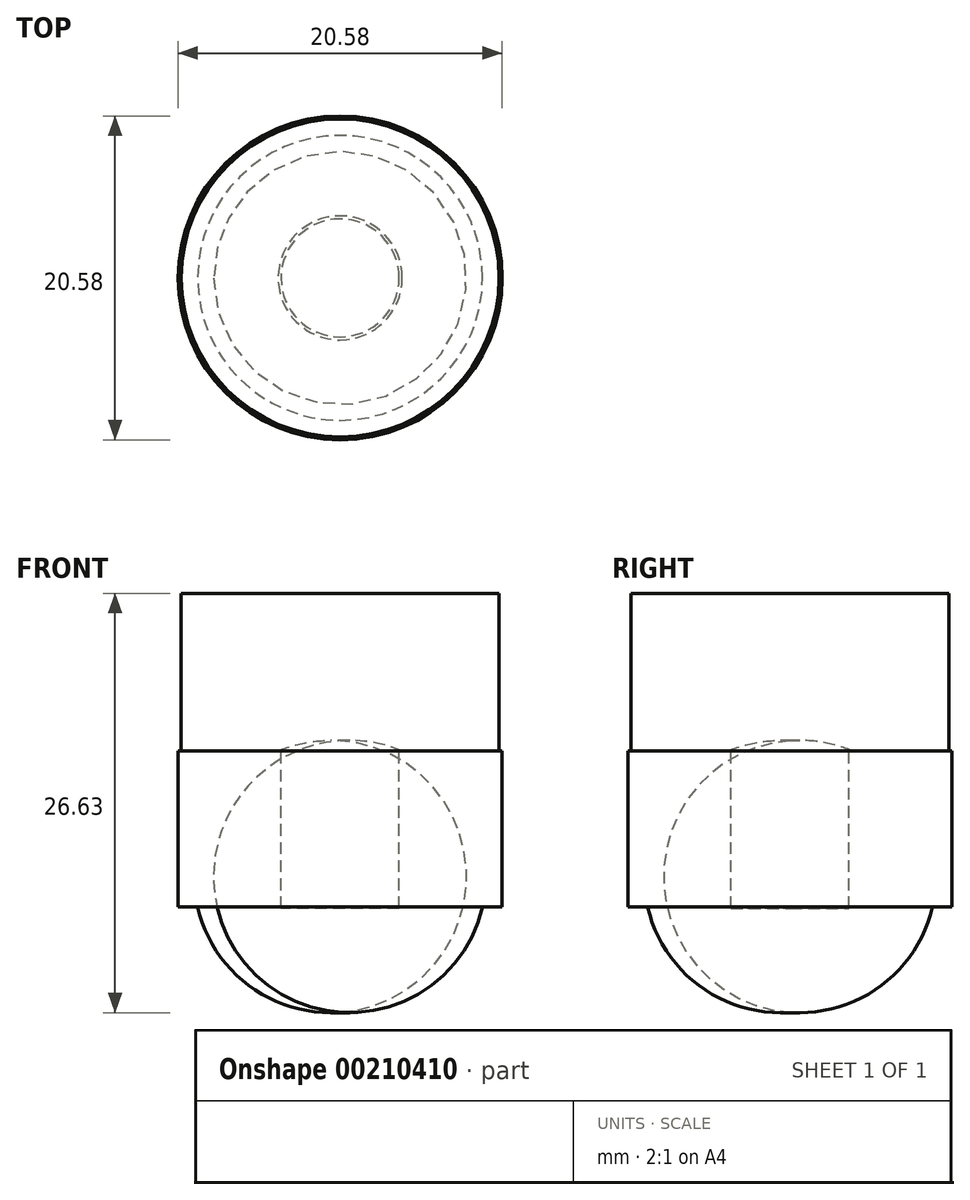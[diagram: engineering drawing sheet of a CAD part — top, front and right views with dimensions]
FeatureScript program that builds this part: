
annotation { "Feature Type Name" : "Feature", "Feature Type Description" : "" }
export const myFeature = defineFeature(function(context is Context, id is Id, definition is map)
    precondition{}
    {
        {
            var Q0;
            Q0=qCreatedBy(makeId("Top.planeOp"),FACE);
            var sketch = newSketch(context, id + "F0", { "sketchPlane" : qUnion([Q0])});
            skCircle(sketch, "E0", {"center": v(0, 0) * mm, "radius": 10.1 * mm});
            skSolve(sketch);
        }
        {
            var Q0;
            Q0=makeQuery(id+"F0.imprint","IMPRINT",FACE,{"disambiguationData":[TD([[makeQuery(id+"F0.imprint","IMPRINT",EDGE,{"derivedFrom":sQuery(id+"F0.wireOp",EDGE,"E0")}),1.0]])]});
            extrude(context, id + "F1", {"entities" : qUnion([Q0]), "depth" : 10 * mm});
        }
        {
            var Q0;
            Q0=qCreatedBy(makeId("Top.planeOp"),FACE);
            var sketch = newSketch(context, id + "F2", { "sketchPlane" : qUnion([Q0])});
            skCircle(sketch, "E1", {"center": v(0, 0) * mm, "radius": 3.75 * mm});
            skSolve(sketch);
        }
        {
            var Q0;
            Q0=makeQuery(id+"F2.imprint","IMPRINT",FACE,{"disambiguationData":[TD([[makeQuery(id+"F2.imprint","IMPRINT",EDGE,{"derivedFrom":sQuery(id+"F2.wireOp",EDGE,"E1")}),1.0]])]});
            var Q1;
            Q1=sQuery(id+"F2.wireOp",EDGE,"E1");
            extrude(context, id + "F3", {"entities" : qUnion([Q0]), "surfaceEntities" : qUnion([Q1]), "oppositeDirection" : true, "depth" : 10 * mm});
        }
        {
            var Q0;
            Q0=qCreatedBy(makeId("Front.planeOp"),FACE);
            var sketch = newSketch(context, id + "F4", { "sketchPlane" : qUnion([Q0])});
            skLineSegment(sketch, "E2", {"start": v(0, 17.84) * mm, "end": v(0, -26.69) * mm, "construction": true});
            skLineSegment(sketch, "E3", {"start": v(-10.3, 0) * mm, "end": v(-10.3, -9.92) * mm});
            skLineSegment(sketch, "E4", {"start": v(-10.3, 0) * mm, "end": v(-3.94, 0) * mm});
            skLineSegment(sketch, "E5", {"start": v(-10.3, -9.92) * mm, "end": v(-9.04, -9.92) * mm});
            skArc(sketch, "E6", {"start": v(-3.94, 0) * mm, "mid": v(-8.3, -4.03) * mm, "end": v(-9.04, -9.92) * mm});
            skSolve(sketch);
        }
        {
            var Q0;
            Q0=makeQuery(id+"F4.imprint","IMPRINT",FACE,{"disambiguationData":[TD([[makeQuery(id+"F4.imprint","IMPRINT",EDGE,{"derivedFrom":sQuery(id+"F4.wireOp",EDGE,"E3")}),1.0]])]});
            var Q1;
            Q1=sQuery(id+"F4.wireOp",EDGE,"E2");
            revolve(context, id + "F5", {"operationType" : NewBodyOperationType.ADD, "entities" : qUnion([Q0]), "axis" : qUnion([Q1]), "revolveType" : RevolveType.FULL});
        }
    });
